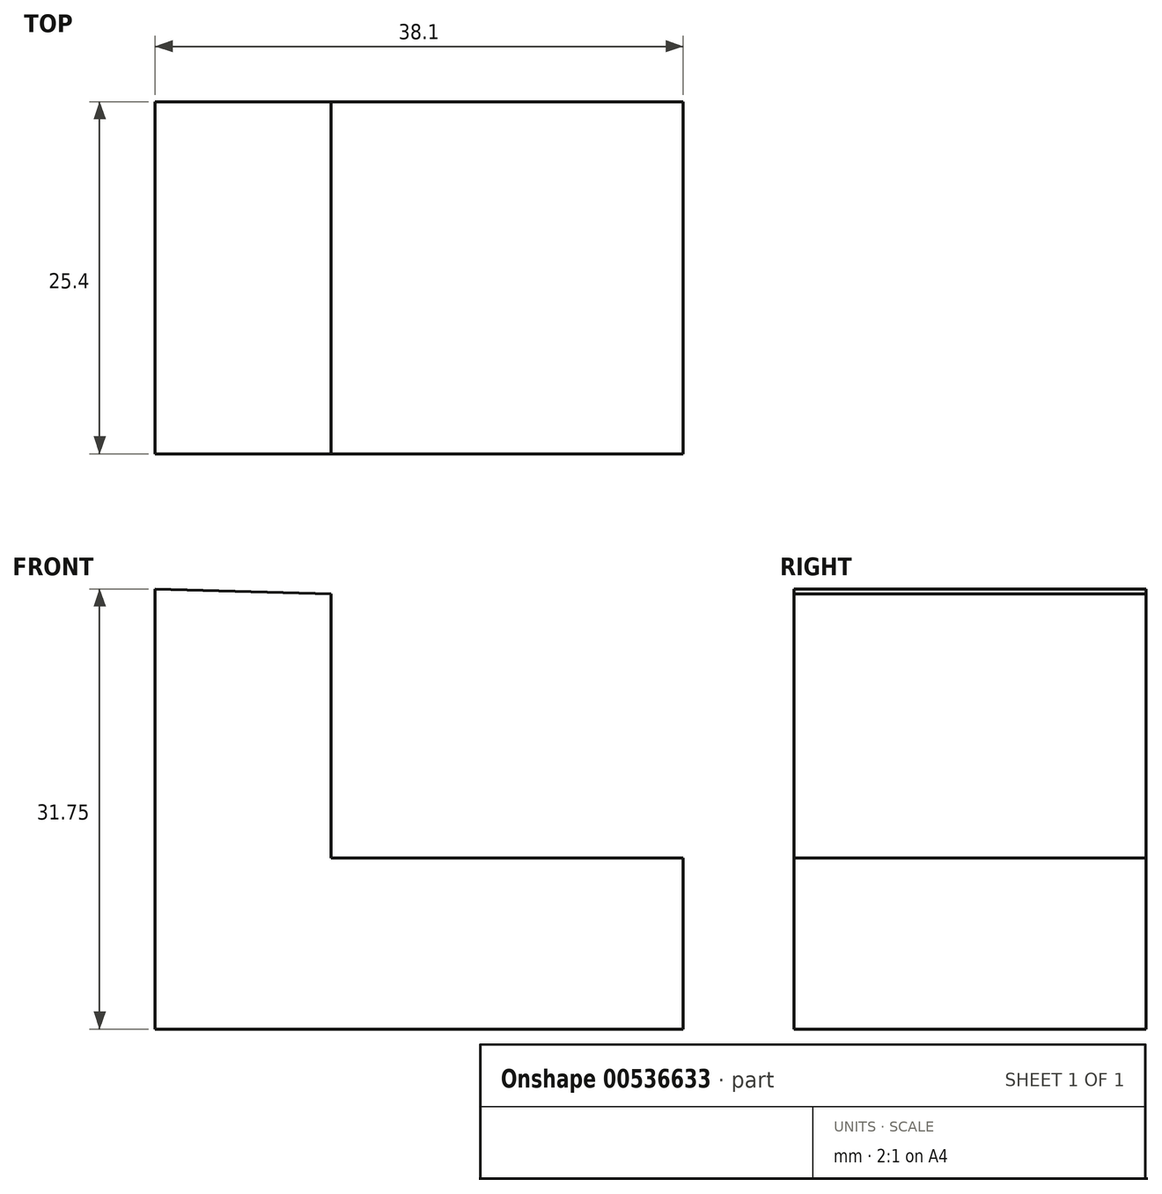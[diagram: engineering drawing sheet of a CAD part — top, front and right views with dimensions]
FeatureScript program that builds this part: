
annotation { "Feature Type Name" : "Feature", "Feature Type Description" : "" }
export const myFeature = defineFeature(function(context is Context, id is Id, definition is map)
    precondition{}
    {
        {
            var Q0;
            Q0=qCreatedBy(makeId("Front.planeOp"),FACE);
            var sketch = newSketch(context, id + "F0", { "sketchPlane" : qUnion([Q0])});
            skLineSegment(sketch, "E0", {"start": v(-54.4, 31.75) * mm, "end": v(-54.4, 0) * mm});
            skLineSegment(sketch, "E1", {"start": v(-54.4, 0) * mm, "end": v(-16.3, 0) * mm});
            skLineSegment(sketch, "E2", {"start": v(-16.31, -0.36) * mm, "end": v(-16.31, 12.34) * mm});
            skLineSegment(sketch, "E3", {"start": v(-16.31, 12.34) * mm, "end": v(-41.71, 12.34) * mm});
            skLineSegment(sketch, "E4", {"start": v(-41.71, 12.34) * mm, "end": v(-41.71, 31.39) * mm});
            skLineSegment(sketch, "E5", {"start": v(-41.71, 31.39) * mm, "end": v(-54.4, 31.75) * mm});
            skSolve(sketch);
        }
        {
            var Q0;
            {var subQ4=sQuery(id+"F0.wireOp",EDGE,"E0");Q0=makeQuery(id+"F0.imprint","IMPRINT",FACE,{"disambiguationData":[TD([[makeQuery(id+"F0.imprint","IMPRINT",EDGE,{"derivedFrom":subQ4}),1.0]])]});}
            extrude(context, id + "F1", {"entities" : qUnion([Q0]), "depth" : 25.4 * mm, "offsetDistance" : 25.4 * mm});
        }
    });
